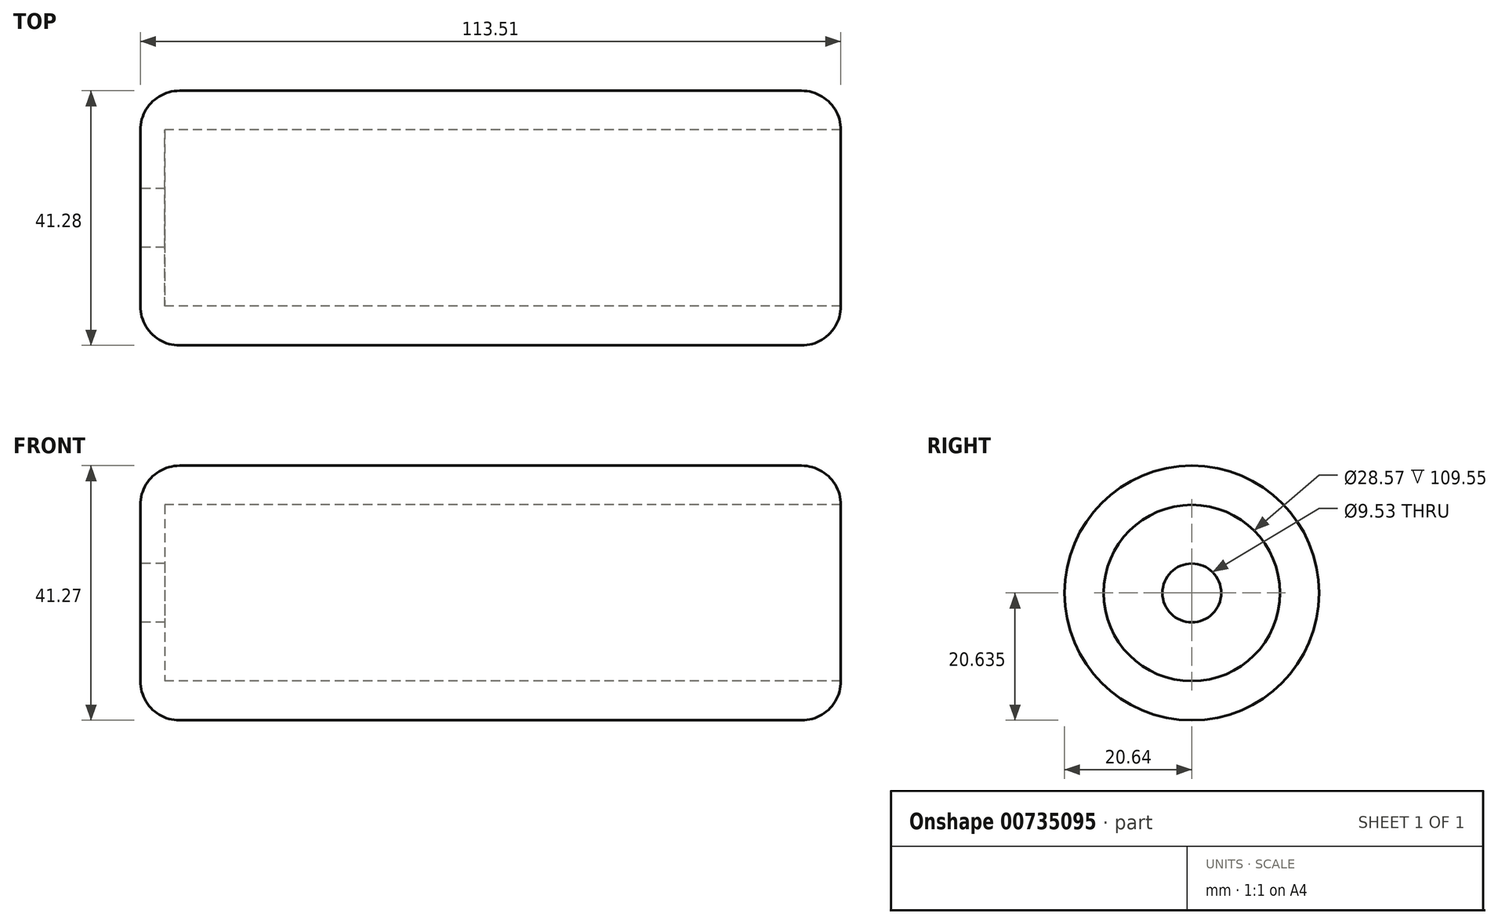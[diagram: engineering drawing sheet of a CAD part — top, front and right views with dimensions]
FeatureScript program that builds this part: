
annotation { "Feature Type Name" : "Feature", "Feature Type Description" : "" }
export const myFeature = defineFeature(function(context is Context, id is Id, definition is map)
    precondition{}
    {
        {
            var Q0;
            Q0=qCreatedBy(makeId("Front.planeOp"),FACE);
            var sketch = newSketch(context, id + "F0", { "sketchPlane" : qUnion([Q0])});
            skLineSegment(sketch, "E0", {"start": v(-48.21, -35.43) * mm, "end": v(65.3, -35.43) * mm});
            skLineSegment(sketch, "E1", {"start": v(65.3, -35.43) * mm, "end": v(65.3, -29.08) * mm});
            skLineSegment(sketch, "E2", {"start": v(65.3, -29.08) * mm, "end": v(-44.25, -29.08) * mm});
            skLineSegment(sketch, "E3", {"start": v(-44.25, -29.08) * mm, "end": v(-44.25, -19.56) * mm});
            skLineSegment(sketch, "E4", {"start": v(-44.25, -19.56) * mm, "end": v(-48.21, -19.56) * mm});
            skLineSegment(sketch, "E5", {"start": v(-48.21, -19.56) * mm, "end": v(-48.21, -35.43) * mm});
            skLineSegment(sketch, "E6", {"start": v(-49.8, -14.8) * mm, "end": v(69.91, -14.8) * mm, "construction": true});
            skSolve(sketch);
        }
        {
            var Q0;
            Q0=qSketchRegion(id+"F0",true);
            var Q1;
            Q1=sQuery(id+"F0.wireOp",EDGE,"E6");
            revolve(context, id + "F1", {"entities" : qUnion([Q0]), "axis" : qUnion([Q1]), "revolveType" : RevolveType.FULL});
        }
        {
            var Q0;
            Q0=makeQuery(id+"F1.opRevolve","SWEPT_EDGE",EDGE,{"disambiguationData":[OSD([sQuery(id+"F0.wireOp",EDGE,"E0"),sQuery(id+"F0.wireOp",EDGE,"E5")])]});
            var Q1;
            Q1=makeQuery(id+"F1.opRevolve","SWEPT_EDGE",EDGE,{"disambiguationData":[OSD([sQuery(id+"F0.wireOp",EDGE,"E0"),sQuery(id+"F0.wireOp",EDGE,"E1")])]});
            fillet(context, id + "F2", {"entities" : qUnion([Q0, Q1]), "radius" : 6.35 * mm, "tangentPropagation" : true, "allowEdgeOverflow" : false});
        }
    });
